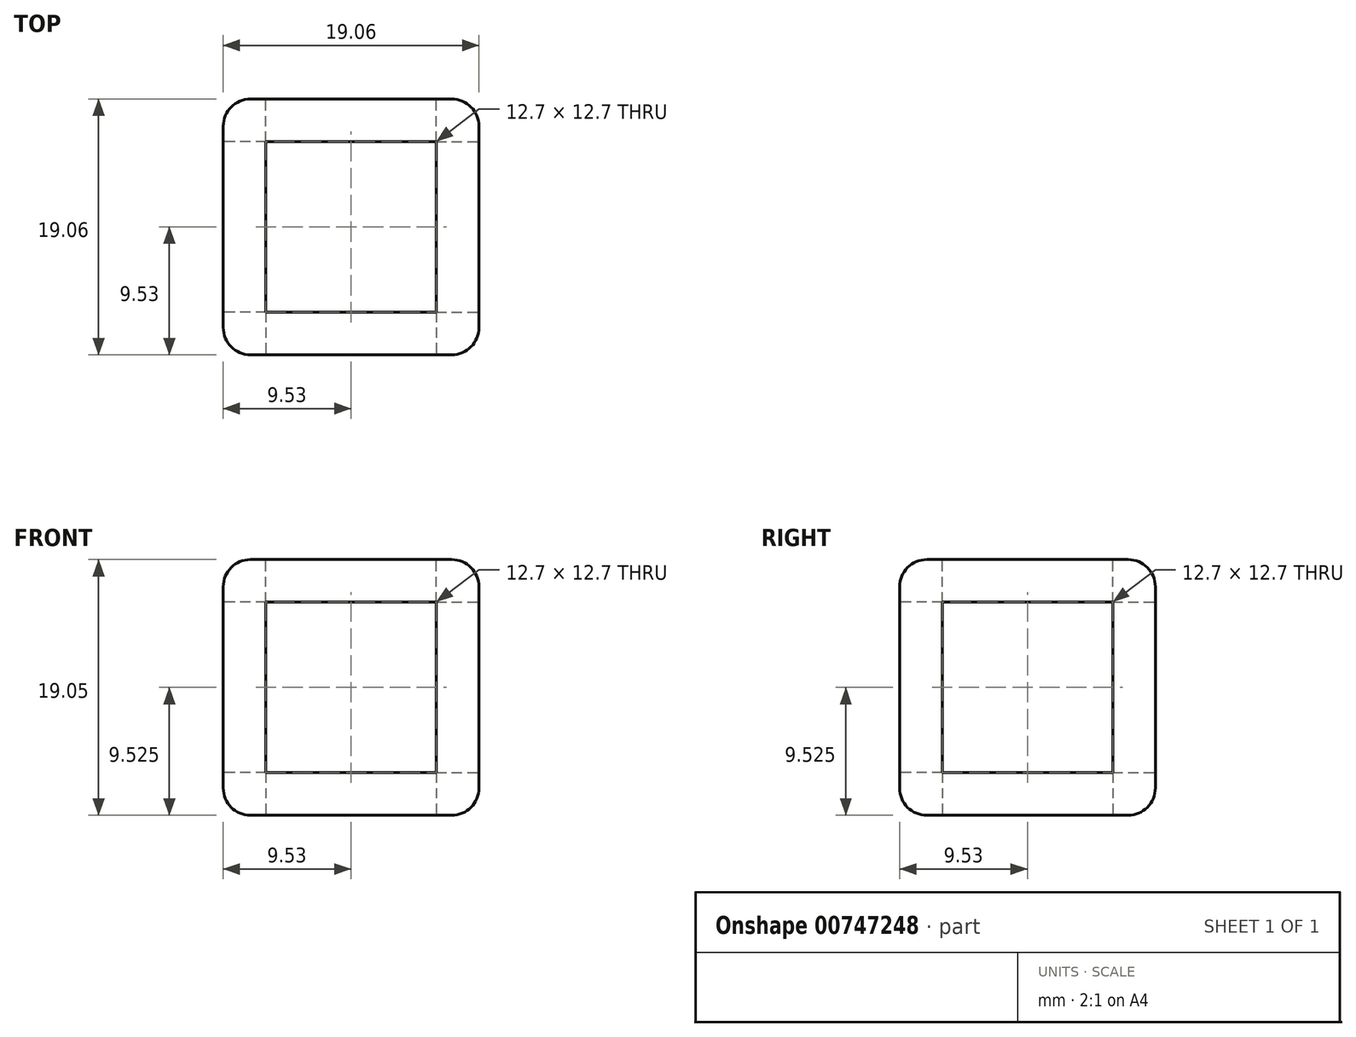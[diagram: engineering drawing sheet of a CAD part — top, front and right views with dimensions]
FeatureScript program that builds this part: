
annotation { "Feature Type Name" : "Feature", "Feature Type Description" : "" }
export const myFeature = defineFeature(function(context is Context, id is Id, definition is map)
    precondition{}
    {
        {
            var Q0;
            Q0=qCreatedBy(makeId("Top.planeOp"),FACE);
            var sketch = newSketch(context, id + "F0", { "sketchPlane" : qUnion([Q0])});
            skLineSegment(sketch, "E0.bottom", {"start": v(-9.53, -9.53) * mm, "end": v(9.53, -9.53) * mm});
            skLineSegment(sketch, "E0.top", {"start": v(-9.53, 9.53) * mm, "end": v(9.53, 9.53) * mm});
            skLineSegment(sketch, "E0.left", {"start": v(-9.53, -9.53) * mm, "end": v(-9.53, 9.53) * mm});
            skLineSegment(sketch, "E0.right", {"start": v(9.53, -9.53) * mm, "end": v(9.53, 9.53) * mm});
            skPoint(sketch, "E0.middle", {"position": v(0, 0) * mm});
            skSolve(sketch);
        }
        {
            var Q0;
            Q0 = qSketchRegion(id + "F0", true);
            extrude(context, id + "F1", {"entities" : qUnion([Q0]), "depth" : 19.05 * mm, "offsetDistance" : 25.4 * mm});
        }
        {
            var Q0;
            Q0=makeQuery(id+"F1.opExtrude","CAP_FACE",FACE,{"disambiguationData":[OSD([sQuery(id+"F0.wireOp",EDGE,"E0.bottom"),sQuery(id+"F0.wireOp",EDGE,"E0.top"),sQuery(id+"F0.wireOp",EDGE,"E0.left"),sQuery(id+"F0.wireOp",EDGE,"E0.right")])],"isStart":false});
            var Q1;
            Q1=makeQuery(id+"F1.opExtrude","SWEPT_FACE",FACE,{"disambiguationData":[OSD([sQuery(id+"F0.wireOp",EDGE,"E0.left")])]});
            var Q2;
            Q2=makeQuery(id+"F1.opExtrude","SWEPT_FACE",FACE,{"disambiguationData":[OSD([sQuery(id+"F0.wireOp",EDGE,"E0.top")])]});
            var Q3;
            Q3=makeQuery(id+"F1.opExtrude","SWEPT_FACE",FACE,{"disambiguationData":[OSD([sQuery(id+"F0.wireOp",EDGE,"E0.bottom")])]});
            var Q4;
            Q4=makeQuery(id+"F1.opExtrude","SWEPT_FACE",FACE,{"disambiguationData":[OSD([sQuery(id+"F0.wireOp",EDGE,"E0.right")])]});
            var Q5;
            Q5=makeQuery(id+"F1.opExtrude","CAP_FACE",FACE,{"disambiguationData":[OSD([sQuery(id+"F0.wireOp",EDGE,"E0.bottom"),sQuery(id+"F0.wireOp",EDGE,"E0.top"),sQuery(id+"F0.wireOp",EDGE,"E0.left"),sQuery(id+"F0.wireOp",EDGE,"E0.right")])],"isStart":true});
            fillet(context, id + "F2", {"entities" : qUnion([Q0, Q1, Q2, Q3, Q4, Q5]), "radius" : 2.03 * mm, "tangentPropagation" : true, "allowEdgeOverflow" : false});
        }
        {
            var Q0;
            Q0=makeQuery(id+"F1.opExtrude","CAP_FACE",FACE,{"disambiguationData":[OSD([sQuery(id+"F0.wireOp",EDGE,"E0.bottom"),sQuery(id+"F0.wireOp",EDGE,"E0.top"),sQuery(id+"F0.wireOp",EDGE,"E0.left"),sQuery(id+"F0.wireOp",EDGE,"E0.right")])],"isStart":false});
            var sketch = newSketch(context, id + "F3", { "sketchPlane" : qUnion([Q0])});
            skLineSegment(sketch, "E1.bottom", {"start": v(-6.35, 6.35) * mm, "end": v(6.35, 6.35) * mm});
            skLineSegment(sketch, "E1.top", {"start": v(-6.35, -6.35) * mm, "end": v(6.35, -6.35) * mm});
            skLineSegment(sketch, "E1.left", {"start": v(-6.35, 6.35) * mm, "end": v(-6.35, -6.35) * mm});
            skLineSegment(sketch, "E1.right", {"start": v(6.35, 6.35) * mm, "end": v(6.35, -6.35) * mm});
            skPoint(sketch, "E1.middle", {"position": v(0, 0) * mm});
            skSolve(sketch);
        }
        {
            var Q0;
            Q0 = qSketchRegion(id + "F3", true);
            extrude(context, id + "F4", {"entities" : qUnion([Q0]), "operationType" : NewBodyOperationType.REMOVE, "oppositeDirection" : true, "depth" : 3.3 * mm, "offsetDistance" : 25.4 * mm});
        }
        {
            var Q0;
            Q0=makeQuery(id+"F1.opExtrude","SWEPT_FACE",FACE,{"disambiguationData":[OSD([sQuery(id+"F0.wireOp",EDGE,"E0.top")])]});
            var sketch = newSketch(context, id + "F5", { "sketchPlane" : qUnion([Q0])});
            skLineSegment(sketch, "E2", {"start": v(0, 17.02) * mm, "end": v(0, 2.03) * mm});
            skLineSegment(sketch, "E3.bottom", {"start": v(-6.35, 15.87) * mm, "end": v(6.35, 15.87) * mm});
            skLineSegment(sketch, "E3.top", {"start": v(-6.35, 3.17) * mm, "end": v(6.35, 3.17) * mm});
            skLineSegment(sketch, "E3.left", {"start": v(-6.35, 15.87) * mm, "end": v(-6.35, 3.17) * mm});
            skLineSegment(sketch, "E3.right", {"start": v(6.35, 15.87) * mm, "end": v(6.35, 3.17) * mm});
            skPoint(sketch, "E3.middle", {"position": v(0, 9.53) * mm});
            skSolve(sketch);
        }
        {
            var Q0;
            Q0 = qSketchRegion(id + "F5", true);
            extrude(context, id + "F6", {"entities" : qUnion([Q0]), "operationType" : NewBodyOperationType.REMOVE, "oppositeDirection" : true, "depth" : 3.3 * mm, "offsetDistance" : 25.4 * mm});
        }
        {
            var Q0;
            Q0=makeQuery(id+"F1.opExtrude","SWEPT_FACE",FACE,{"disambiguationData":[OSD([sQuery(id+"F0.wireOp",EDGE,"E0.left")])]});
            var sketch = newSketch(context, id + "F7", { "sketchPlane" : qUnion([Q0])});
            skLineSegment(sketch, "E4", {"start": v(0, 17.02) * mm, "end": v(0, 2.03) * mm});
            skLineSegment(sketch, "E5.bottom", {"start": v(-6.35, 15.88) * mm, "end": v(6.35, 15.88) * mm});
            skLineSegment(sketch, "E5.top", {"start": v(-6.35, 3.17) * mm, "end": v(6.35, 3.17) * mm});
            skLineSegment(sketch, "E5.left", {"start": v(-6.35, 15.88) * mm, "end": v(-6.35, 3.17) * mm});
            skLineSegment(sketch, "E5.right", {"start": v(6.35, 15.88) * mm, "end": v(6.35, 3.17) * mm});
            skPoint(sketch, "E5.middle", {"position": v(0, 9.53) * mm});
            skSolve(sketch);
        }
        {
            var Q0;
            Q0 = qSketchRegion(id + "F7", true);
            extrude(context, id + "F8", {"entities" : qUnion([Q0]), "operationType" : NewBodyOperationType.REMOVE, "oppositeDirection" : true, "depth" : 3.3 * mm, "offsetDistance" : 25.4 * mm});
        }
        {
            var Q0;
            Q0=makeQuery(id+"F1.opExtrude","SWEPT_FACE",FACE,{"disambiguationData":[OSD([sQuery(id+"F0.wireOp",EDGE,"E0.bottom")])]});
            var sketch = newSketch(context, id + "F9", { "sketchPlane" : qUnion([Q0])});
            skLineSegment(sketch, "E6", {"start": v(0, 17.02) * mm, "end": v(0, 2.03) * mm});
            skLineSegment(sketch, "E7.bottom", {"start": v(-6.35, 15.88) * mm, "end": v(6.35, 15.88) * mm});
            skLineSegment(sketch, "E7.top", {"start": v(-6.35, 3.18) * mm, "end": v(6.35, 3.18) * mm});
            skLineSegment(sketch, "E7.left", {"start": v(-6.35, 15.88) * mm, "end": v(-6.35, 3.18) * mm});
            skLineSegment(sketch, "E7.right", {"start": v(6.35, 15.88) * mm, "end": v(6.35, 3.18) * mm});
            skPoint(sketch, "E7.middle", {"position": v(0, 9.53) * mm});
            skSolve(sketch);
        }
        {
            var Q0;
            Q0 = qSketchRegion(id + "F9", true);
            extrude(context, id + "F10", {"entities" : qUnion([Q0]), "operationType" : NewBodyOperationType.REMOVE, "oppositeDirection" : true, "depth" : 3.3 * mm, "offsetDistance" : 25.4 * mm});
        }
        {
            var Q0;
            Q0=makeQuery(id+"F1.opExtrude","SWEPT_FACE",FACE,{"disambiguationData":[OSD([sQuery(id+"F0.wireOp",EDGE,"E0.right")])]});
            var sketch = newSketch(context, id + "F11", { "sketchPlane" : qUnion([Q0])});
            skLineSegment(sketch, "E8", {"start": v(0, 2.03) * mm, "end": v(0, 17.02) * mm});
            skLineSegment(sketch, "E9.bottom", {"start": v(-6.35, 15.88) * mm, "end": v(6.35, 15.88) * mm});
            skLineSegment(sketch, "E9.top", {"start": v(-6.35, 3.18) * mm, "end": v(6.35, 3.18) * mm});
            skLineSegment(sketch, "E9.left", {"start": v(-6.35, 15.88) * mm, "end": v(-6.35, 3.18) * mm});
            skLineSegment(sketch, "E9.right", {"start": v(6.35, 15.88) * mm, "end": v(6.35, 3.17) * mm});
            skPoint(sketch, "E9.middle", {"position": v(0, 9.53) * mm});
            skSolve(sketch);
        }
        {
            var Q0;
            Q0 = qSketchRegion(id + "F11", true);
            extrude(context, id + "F12", {"entities" : qUnion([Q0]), "operationType" : NewBodyOperationType.REMOVE, "oppositeDirection" : true, "depth" : 3.3 * mm, "offsetDistance" : 25.4 * mm});
        }
        {
            var Q0;
            Q0=makeQuery(id+"F1.opExtrude","CAP_FACE",FACE,{"disambiguationData":[OSD([sQuery(id+"F0.wireOp",EDGE,"E0.bottom"),sQuery(id+"F0.wireOp",EDGE,"E0.top"),sQuery(id+"F0.wireOp",EDGE,"E0.left"),sQuery(id+"F0.wireOp",EDGE,"E0.right")])],"isStart":true});
            var sketch = newSketch(context, id + "F13", { "sketchPlane" : qUnion([Q0])});
            skLineSegment(sketch, "E10", {"start": v(0, 7.5) * mm, "end": v(0, -7.5) * mm});
            skLineSegment(sketch, "E11.bottom", {"start": v(-6.35, 6.35) * mm, "end": v(6.35, 6.35) * mm});
            skLineSegment(sketch, "E11.top", {"start": v(-6.35, -6.35) * mm, "end": v(6.35, -6.35) * mm});
            skLineSegment(sketch, "E11.left", {"start": v(-6.35, 6.35) * mm, "end": v(-6.35, -6.35) * mm});
            skLineSegment(sketch, "E11.right", {"start": v(6.35, 6.35) * mm, "end": v(6.35, -6.35) * mm});
            skPoint(sketch, "E11.middle", {"position": v(0, 0) * mm});
            skSolve(sketch);
        }
        {
            var Q0;
            Q0 = qSketchRegion(id + "F13", true);
            extrude(context, id + "F14", {"entities" : qUnion([Q0]), "operationType" : NewBodyOperationType.REMOVE, "oppositeDirection" : true, "depth" : 41.15 * mm, "offsetDistance" : 25.4 * mm});
        }
    });
